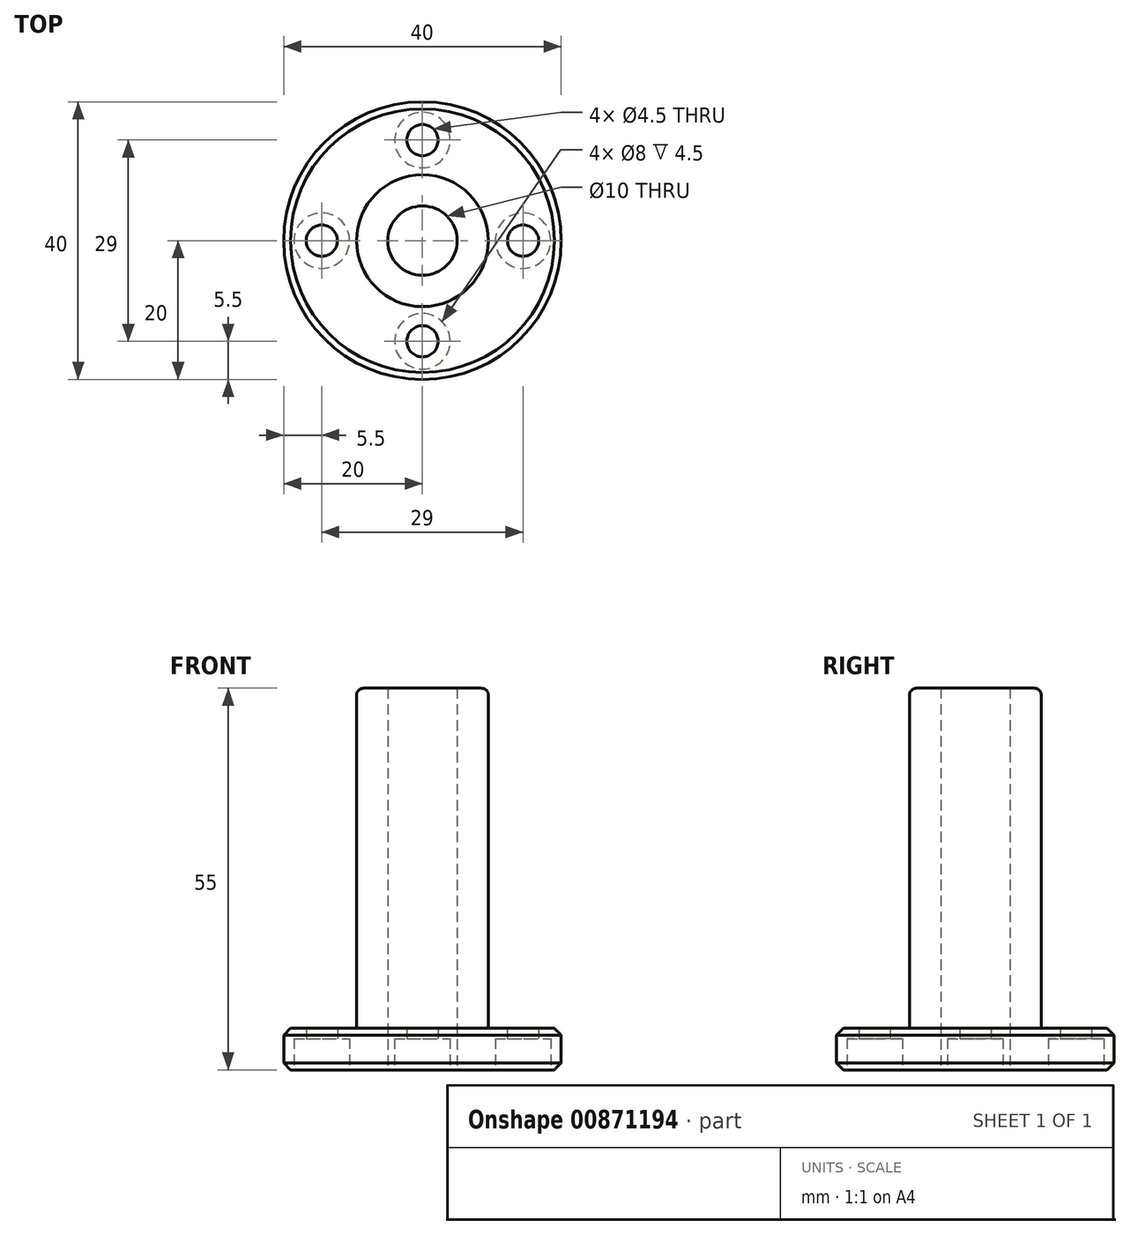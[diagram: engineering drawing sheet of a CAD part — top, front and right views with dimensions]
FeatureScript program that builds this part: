
annotation { "Feature Type Name" : "Feature", "Feature Type Description" : "" }
export const myFeature = defineFeature(function(context is Context, id is Id, definition is map)
    precondition{}
    {
        {
            var Q0;
            Q0=qCreatedBy(makeId("Top.planeOp"),FACE);
            var sketch = newSketch(context, id + "F0", { "sketchPlane" : qUnion([Q0])});
            skCircle(sketch, "E0", {"center": v(0, 0) * mm, "radius": 20 * mm});
            skCircle(sketch, "E1", {"center": v(0, 0) * mm, "radius": 5 * mm});
            skCircle(sketch, "E2", {"center": v(0, 0) * mm, "radius": 14.5 * mm, "construction": true});
            skCircle(sketch, "E3", {"center": v(0, 14.5) * mm, "radius": 2.25 * mm});
            skCircle(sketch, "E4", {"center": v(-14.5, 0) * mm, "radius": 2.25 * mm});
            skCircle(sketch, "E5", {"center": v(0, -14.5) * mm, "radius": 2.25 * mm});
            skCircle(sketch, "E6", {"center": v(14.5, 0) * mm, "radius": 2.25 * mm});
            skSolve(sketch);
        }
        {
            var Q0;
            Q0 = qSketchRegion(id + "F0", true);
            extrude(context, id + "F1", {"entities" : qUnion([Q0]), "depth" : 6 * mm, "offsetDistance" : 25 * mm});
        }
        {
            var Q0;
            Q0=makeQuery(id+"F1.opExtrude","CAP_FACE",FACE,{"disambiguationData":[OSD([sQuery(id+"F0.wireOp",EDGE,"E0"),sQuery(id+"F0.wireOp",EDGE,"E1"),sQuery(id+"F0.wireOp",EDGE,"E3"),sQuery(id+"F0.wireOp",EDGE,"E4"),sQuery(id+"F0.wireOp",EDGE,"E5"),sQuery(id+"F0.wireOp",EDGE,"E6")])],"isStart":false});
            var sketch = newSketch(context, id + "F2", { "sketchPlane" : qUnion([Q0])});
            skCircle(sketch, "E7", {"center": v(0, 0) * mm, "radius": 9.5 * mm});
            skSolve(sketch);
        }
        {
            var Q0;
            Q0=makeQuery(id+"F2.imprint","IMPRINT",FACE,{"disambiguationData":[TD([[makeQuery(id+"F2.imprint","IMPRINT",EDGE,{"derivedFrom":sQuery(id+"F2.wireOp",EDGE,"E7")}),1.0]])]});
            extrude(context, id + "F3", {"entities" : qUnion([Q0]), "operationType" : NewBodyOperationType.ADD, "depth" : 49 * mm, "offsetDistance" : 25 * mm});
        }
        {
            var Q0;
            Q0=makeQuery(id+"F1.opExtrude","CAP_FACE",FACE,{"disambiguationData":[OSD([sQuery(id+"F0.wireOp",EDGE,"E0"),sQuery(id+"F0.wireOp",EDGE,"E1"),sQuery(id+"F0.wireOp",EDGE,"E3"),sQuery(id+"F0.wireOp",EDGE,"E4"),sQuery(id+"F0.wireOp",EDGE,"E5"),sQuery(id+"F0.wireOp",EDGE,"E6")])],"isStart":true});
            var sketch = newSketch(context, id + "F4", { "sketchPlane" : qUnion([Q0])});
            skCircle(sketch, "E8", {"center": v(0, 14.5) * mm, "radius": 4 * mm});
            skCircle(sketch, "E9", {"center": v(14.5, 0) * mm, "radius": 4 * mm});
            skCircle(sketch, "E10", {"center": v(0, -14.5) * mm, "radius": 4 * mm});
            skCircle(sketch, "E11", {"center": v(-14.5, 0) * mm, "radius": 4 * mm});
            skSolve(sketch);
        }
        {
            var Q0;
            Q0 = qSketchRegion(id + "F4", true);
            extrude(context, id + "F5", {"entities" : qUnion([Q0]), "operationType" : NewBodyOperationType.REMOVE, "oppositeDirection" : true, "depth" : 4.5 * mm, "offsetDistance" : 25 * mm});
        }
        {
            var Q0;
            Q0=makeQuery(id+"F1.opExtrude","CAP_EDGE",EDGE,{"disambiguationData":[OSD([sQuery(id+"F0.wireOp",EDGE,"E0")])],"isStart":true});
            var Q1;
            Q1=makeQuery(id+"F1.opExtrude","CAP_EDGE",EDGE,{"disambiguationData":[OSD([sQuery(id+"F0.wireOp",EDGE,"E0")])],"isStart":false});
            chamfer(context, id + "F6", {"entities" : qUnion([Q0, Q1]), "width" : 1 * mm, "tangentPropagation" : true});
        }
        {
            var Q0;
            Q0=makeQuery(id+"F3.opExtrude","CAP_EDGE",EDGE,{"disambiguationData":[OSD([sQuery(id+"F2.wireOp",EDGE,"E7")])],"isStart":false});
            fillet(context, id + "F7", {"entities" : qUnion([Q0]), "radius" : 1 * mm, "tangentPropagation" : true, "allowEdgeOverflow" : false});
        }
    });
